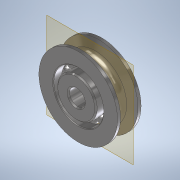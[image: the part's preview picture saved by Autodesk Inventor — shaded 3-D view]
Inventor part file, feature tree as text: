
AUTODESK INVENTOR PART (.ipt)
format: ipt  version: 2020 (Build 240168000, 168)  size: 734,208 bytes
history: native  units: in
note: dims shown in document units (in); Inventor stores cm internally (conversion verified against a paired STEP export)
features: other x14, chamfer x2, revolve x1
ambient origin geometry x8: Origin, YZ Plane, XZ Plane, XY Plane, X Axis, Y Axis, Z Axis, Center Point
bodies: Solid1 (feature_tree), Solid2 (feature_tree), Solid3 (feature_tree), Solid4 (feature_tree), Solid5 (feature_tree), Solid6 (feature_tree), Solid7 (feature_tree), Solid8 (feature_tree), Solid9 (feature_tree), Solid10 (feature_tree), Solid11 (feature_tree), Solid12 (feature_tree), Solid13 (feature_tree), Solid14 (feature_tree), Solid15 (feature_tree), Solid16 (feature_tree), Solid17 (feature_tree)
feature tree (17):
  chamfer  "Chamfer2"  [1 undecoded]
  chamfer  "Chamfer1"  [1 undecoded]
  revolve  "Revolve2"  [1 undecoded]
  other  "CirPattern1[1]"
  other  "CirPattern1[2]"
  other  "CirPattern1[3]"
  other  "CirPattern1[4]"
  other  "CirPattern1[5]"
  other  "CirPattern1[6]"
  other  "CirPattern1[7]"
  other  "CirPattern1[8]"
  other  "CirPattern1[9]"
  other  "CirPattern1[10]"
  other  "CirPattern1[11]"
  other  "CirPattern1[12]"
  other  "CirPattern1[13]"
  other  "CirPattern1[14]"
note: 3 required parameter values undecoded (feature->parameter linkage not recoverable at this tier; creation-order binding heuristic only, values carry confidence <= 0.55)
